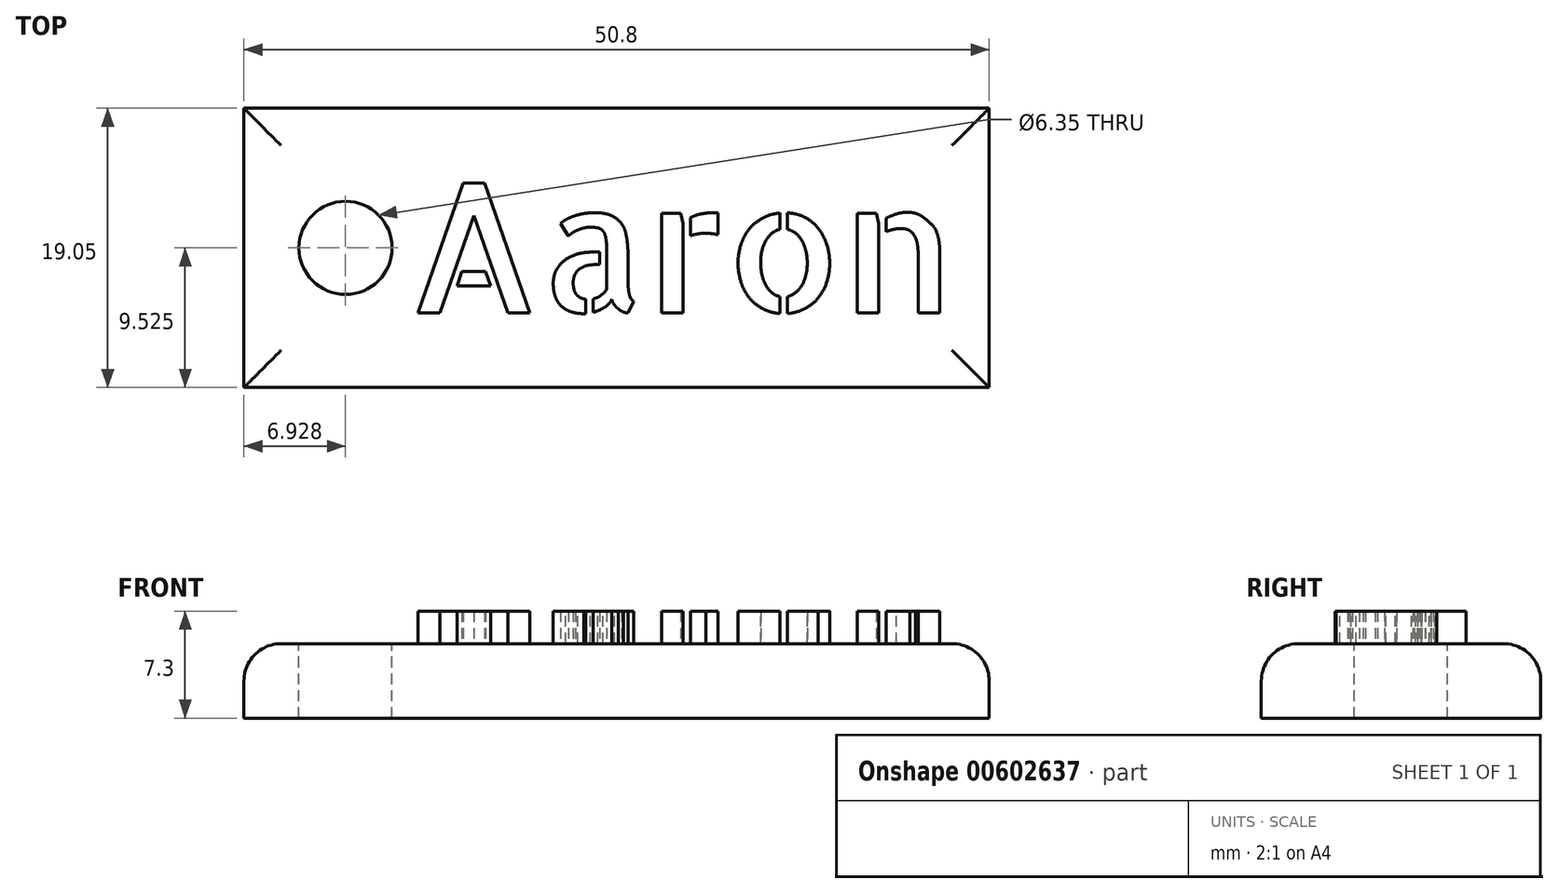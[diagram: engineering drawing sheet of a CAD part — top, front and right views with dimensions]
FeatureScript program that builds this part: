
annotation { "Feature Type Name" : "Feature", "Feature Type Description" : "" }
export const myFeature = defineFeature(function(context is Context, id is Id, definition is map)
    precondition{}
    {
        {
            var Q0;
            Q0=qCreatedBy(makeId("Top.planeOp"),FACE);
            var sketch = newSketch(context, id + "F0", { "sketchPlane" : qUnion([Q0])});
            skLineSegment(sketch, "E0.bottom", {"start": v(0, 19.05) * mm, "end": v(50.8, 19.05) * mm});
            skLineSegment(sketch, "E0.top", {"start": v(0, 0) * mm, "end": v(50.8, 0) * mm});
            skLineSegment(sketch, "E0.left", {"start": v(0, 19.05) * mm, "end": v(0, 0) * mm});
            skLineSegment(sketch, "E0.right", {"start": v(50.8, 19.05) * mm, "end": v(50.8, 0) * mm});
            skSolve(sketch);
        }
        {
            var Q0;
            Q0=makeQuery(id+"F0.imprint","IMPRINT",FACE,{"disambiguationData":[TD([[makeQuery(id+"F0.imprint","IMPRINT",EDGE,{"derivedFrom":sQuery(id+"F0.wireOp",EDGE,"E0.bottom")}),-1.0]])]});
            extrude(context, id + "F1", {"entities" : qUnion([Q0]), "depth" : 5.08 * mm, "offsetDistance" : 25.4 * mm});
        }
        {
            var Q0;
            Q0=makeQuery(id+"F1.opExtrude","CAP_FACE",FACE,{"disambiguationData":[OSD([sQuery(id+"F0.wireOp",EDGE,"E0.bottom"),sQuery(id+"F0.wireOp",EDGE,"E0.top"),sQuery(id+"F0.wireOp",EDGE,"E0.left"),sQuery(id+"F0.wireOp",EDGE,"E0.right")])],"isStart":false});
            var sketch = newSketch(context, id + "F2", { "sketchPlane" : qUnion([Q0])});
            skText(sketch, "E1", { "text": "Aaron", "fontName": "AllertaStencil-Regular.ttf"});
            skLineSegment(sketch, "E2", {"start": v(48.26, 9.53) * mm, "end": v(50.8, 9.53) * mm});
            const initialGuessF2  = {"E1": [0.0111, 0.0051, 1, 0, 0.00887]};
            skSetInitialGuess(sketch, initialGuessF2);
            skSolve(sketch);
        }
        {
            var Q0;
            Q0 = qSketchRegion(id + "F2", true);
            extrude(context, id + "F3", {"entities" : qUnion([Q0]), "operationType" : NewBodyOperationType.ADD, "depth" : 2.22 * mm, "offsetDistance" : 25.4 * mm});
        }
        {
            var Q0;
            Q0=makeQuery(id+"F1.opExtrude","CAP_FACE",FACE,{"disambiguationData":[OSD([sQuery(id+"F0.wireOp",EDGE,"E0.bottom"),sQuery(id+"F0.wireOp",EDGE,"E0.top"),sQuery(id+"F0.wireOp",EDGE,"E0.left"),sQuery(id+"F0.wireOp",EDGE,"E0.right")])],"isStart":false});
            var sketch = newSketch(context, id + "F4", { "sketchPlane" : qUnion([Q0])});
            skCircle(sketch, "E3", {"center": v(6.93, 9.53) * mm, "radius": 3.88 * mm});
            skPoint(sketch, "E3.centerSnap0", {"position": v(0, 9.53) * mm});
            skSolve(sketch);
        }
        {
            var Q0;
            Q0=sQuery(id+"F4.wireOp",EDGE,"E3");
            extrude(context, id + "F5", {"bodyType" : ToolBodyType.SURFACE, "surfaceEntities" : qUnion([Q0]), "depth" : -50.8 * mm, "offsetDistance" : 25.4 * mm});
        }
        {
            var Q0;
            Q0=makeQuery(id+"F5.opExtrude","SWEPT_BODY",BODY,{"disambiguationData":[OSD([sQuery(id+"F4.wireOp",EDGE,"E3")])]});
            deleteBodies(context, id + "F6", {"entities" : qUnion([Q0])});
        }
        {
            var Q0;
            Q0=sQuery(id+"F4.wireOp",VERTEX,"E3.center");
            var Q1;
            Q1=makeQuery(id+"F1.opExtrude","SWEPT_BODY",BODY,{"disambiguationData":[OSD([sQuery(id+"F0.wireOp",EDGE,"E0.bottom"),sQuery(id+"F0.wireOp",EDGE,"E0.top"),sQuery(id+"F0.wireOp",EDGE,"E0.left"),sQuery(id+"F0.wireOp",EDGE,"E0.right")])]});
            hole(context, id + "F7", {"style" : HoleStyle.SIMPLE, "endStyle" : HoleEndStyle.THROUGH, "holeDiameter" : 6.35 * mm, "majorDiameter" : 6.35 * mm, "isTappedThrough" : true, "tappedDepth" : 12.7 * mm, "tapClearance" : 3, "locations" : qUnion([Q0]), "scope" : qUnion([Q1])});
        }
        {
            var Q0;
            Q0=makeQuery(id+"F1.opExtrude","CAP_EDGE",EDGE,{"disambiguationData":[OSD([sQuery(id+"F0.wireOp",EDGE,"E0.bottom")])],"isStart":false});
            var Q1;
            Q1=makeQuery(id+"F1.opExtrude","CAP_EDGE",EDGE,{"disambiguationData":[OSD([sQuery(id+"F0.wireOp",EDGE,"E0.left")])],"isStart":false});
            var Q2;
            Q2=makeQuery(id+"F1.opExtrude","CAP_EDGE",EDGE,{"disambiguationData":[OSD([sQuery(id+"F0.wireOp",EDGE,"E0.top")])],"isStart":false});
            var Q3;
            Q3=makeQuery(id+"F1.opExtrude","CAP_EDGE",EDGE,{"disambiguationData":[OSD([sQuery(id+"F0.wireOp",EDGE,"E0.right")])],"isStart":false});
            fillet(context, id + "F8", {"entities" : qUnion([Q0, Q1, Q2, Q3]), "radius" : 2.54 * mm, "tangentPropagation" : true, "allowEdgeOverflow" : false});
        }
    });
